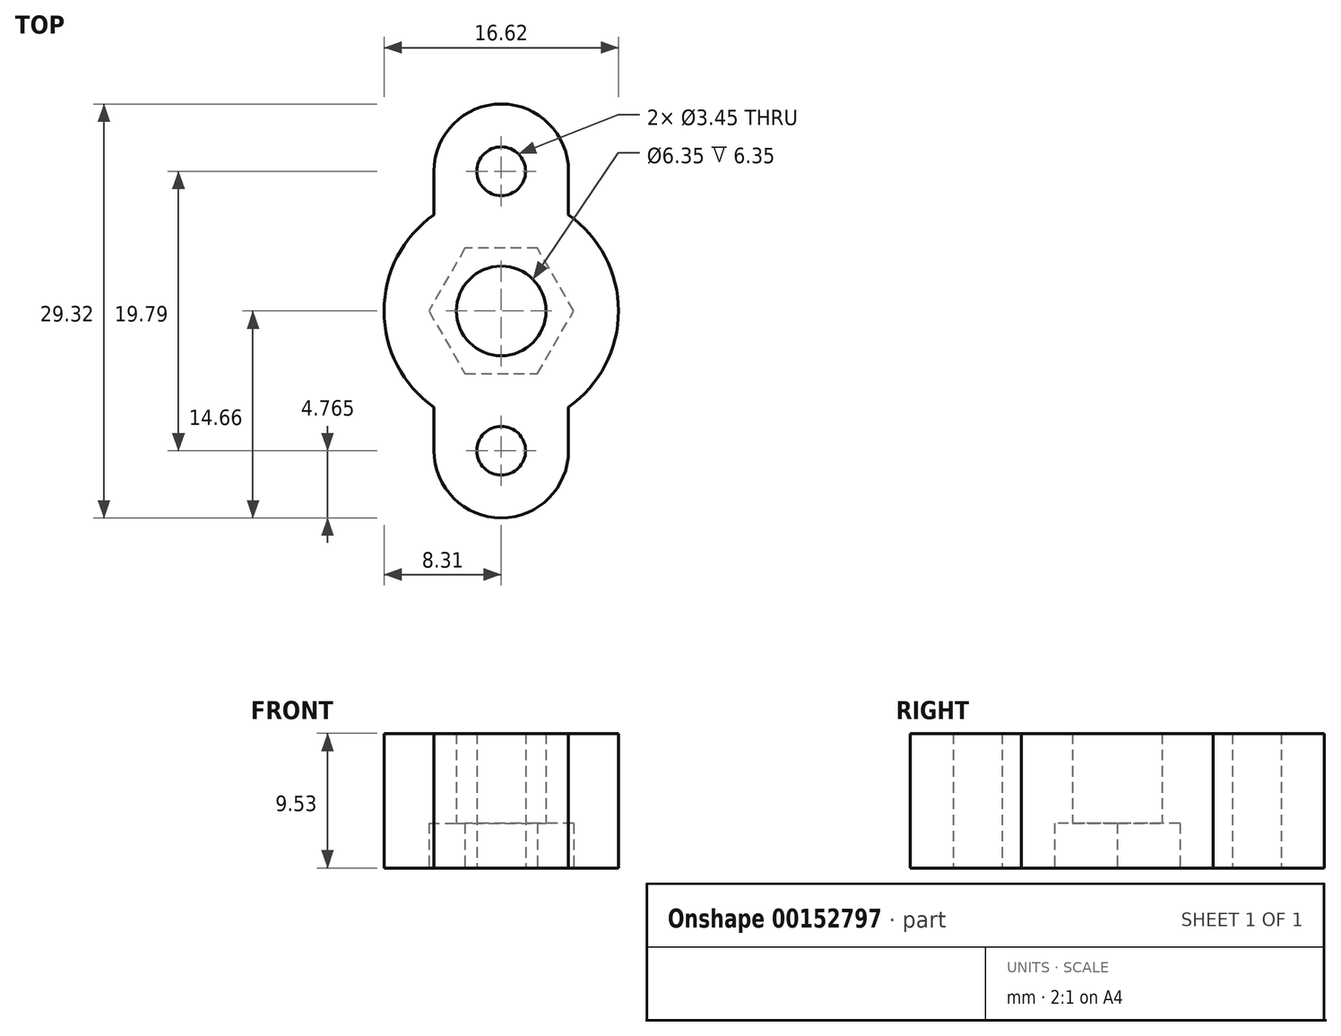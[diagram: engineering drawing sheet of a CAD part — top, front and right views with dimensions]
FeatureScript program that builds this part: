
annotation { "Feature Type Name" : "Feature", "Feature Type Description" : "" }
export const myFeature = defineFeature(function(context is Context, id is Id, definition is map)
    precondition{}
    {
        {
            var Q0;
            Q0=qCreatedBy(makeId("Top.planeOp"),FACE);
            var sketch = newSketch(context, id + "F0", { "sketchPlane" : qUnion([Q0])});
            skCircle(sketch, "E0.cCircle", {"center": v(0, 0) * mm, "radius": 5.13 * mm, "construction": true});
            skLineSegment(sketch, "E0.0", {"start": v(0, 5.13) * mm, "end": v(4.45, 2.57) * mm, "construction": true});
            skLineSegment(sketch, "E0.1", {"start": v(4.45, 2.57) * mm, "end": v(4.45, -2.57) * mm, "construction": true});
            skLineSegment(sketch, "E0.2", {"start": v(4.45, -2.57) * mm, "end": v(0, -5.13) * mm, "construction": true});
            skLineSegment(sketch, "E0.3", {"start": v(0, -5.13) * mm, "end": v(-4.44, -2.57) * mm, "construction": true});
            skLineSegment(sketch, "E0.4", {"start": v(-4.44, -2.57) * mm, "end": v(-4.45, 2.57) * mm, "construction": true});
            skLineSegment(sketch, "E0.5", {"start": v(-4.45, 2.57) * mm, "end": v(0, 5.13) * mm, "construction": true});
            skLineSegment(sketch, "E1", {"start": v(0, -9.9) * mm, "end": v(0, 9.9) * mm, "construction": true});
            skArc(sketch, "E2", {"start": v(-4.76, 6.8) * mm, "mid": v(-8.3, 0) * mm, "end": v(-4.76, -6.8) * mm});
            skArc(sketch, "E3", {"start": v(4.76, -6.8) * mm, "mid": v(8.3, 0) * mm, "end": v(4.76, 6.8) * mm});
            skArc(sketch, "E4", {"start": v(-4.76, -9.9) * mm, "mid": v(0, -14.66) * mm, "end": v(4.76, -9.9) * mm});
            skArc(sketch, "E5", {"start": v(4.76, 9.9) * mm, "mid": v(0, 14.66) * mm, "end": v(-4.76, 9.9) * mm});
            skLineSegment(sketch, "E6", {"start": v(-4.76, -9.9) * mm, "end": v(4.76, -9.9) * mm, "construction": true});
            skLineSegment(sketch, "E7", {"start": v(4.76, 9.9) * mm, "end": v(-4.76, 9.9) * mm, "construction": true});
            skLineSegment(sketch, "E8", {"start": v(-4.76, -9.9) * mm, "end": v(-4.76, -6.8) * mm});
            skLineSegment(sketch, "E9", {"start": v(-4.76, 9.9) * mm, "end": v(-4.76, 6.8) * mm});
            skLineSegment(sketch, "E10", {"start": v(4.76, 9.9) * mm, "end": v(4.76, 6.8) * mm});
            skLineSegment(sketch, "E11", {"start": v(4.76, -9.9) * mm, "end": v(4.76, -6.8) * mm});
            skCircle(sketch, "E12", {"center": v(0, -9.9) * mm, "radius": 1.73 * mm});
            skCircle(sketch, "E13", {"center": v(0, 9.9) * mm, "radius": 1.73 * mm});
            skCircle(sketch, "E14", {"center": v(0, 0) * mm, "radius": 3.18 * mm});
            skSolve(sketch);
        }
        {
            var Q0;
            Q0 = qSketchRegion(id + "F0", true);
            extrude(context, id + "F1", {"entities" : qUnion([Q0]), "depth" : 9.52 * mm});
        }
        {
            var Q0;
            Q0=makeQuery(id+"F1.opExtrude","CAP_FACE",FACE,{"disambiguationData":[OSD([sQuery(id+"F0.wireOp",EDGE,"E2"),sQuery(id+"F0.wireOp",EDGE,"E3"),sQuery(id+"F0.wireOp",EDGE,"E4"),sQuery(id+"F0.wireOp",EDGE,"E5"),sQuery(id+"F0.wireOp",EDGE,"E8"),sQuery(id+"F0.wireOp",EDGE,"E9"),sQuery(id+"F0.wireOp",EDGE,"E10"),sQuery(id+"F0.wireOp",EDGE,"E11"),sQuery(id+"F0.wireOp",EDGE,"E12"),sQuery(id+"F0.wireOp",EDGE,"E13"),sQuery(id+"F0.wireOp",EDGE,"E14")])],"isStart":true});
            var sketch = newSketch(context, id + "F2", { "sketchPlane" : qUnion([Q0])});
            skCircle(sketch, "E15.cCircle", {"center": v(0, 0) * mm, "radius": 5.13 * mm, "construction": true});
            skLineSegment(sketch, "E15.0", {"start": v(-5.13, 0) * mm, "end": v(-2.57, 4.44) * mm});
            skLineSegment(sketch, "E15.1", {"start": v(-2.57, 4.45) * mm, "end": v(2.57, 4.45) * mm});
            skLineSegment(sketch, "E15.2", {"start": v(2.57, 4.44) * mm, "end": v(5.13, 0) * mm});
            skLineSegment(sketch, "E15.3", {"start": v(5.13, 0) * mm, "end": v(2.57, -4.44) * mm});
            skLineSegment(sketch, "E15.4", {"start": v(2.57, -4.44) * mm, "end": v(-2.57, -4.45) * mm});
            skLineSegment(sketch, "E15.5", {"start": v(-2.57, -4.45) * mm, "end": v(-5.13, 0) * mm});
            skSolve(sketch);
        }
        {
            var Q0;
            Q0 = qSketchRegion(id + "F2", true);
            extrude(context, id + "F3", {"entities" : qUnion([Q0]), "operationType" : NewBodyOperationType.REMOVE, "oppositeDirection" : true, "depth" : 3.17 * mm});
        }
    });
